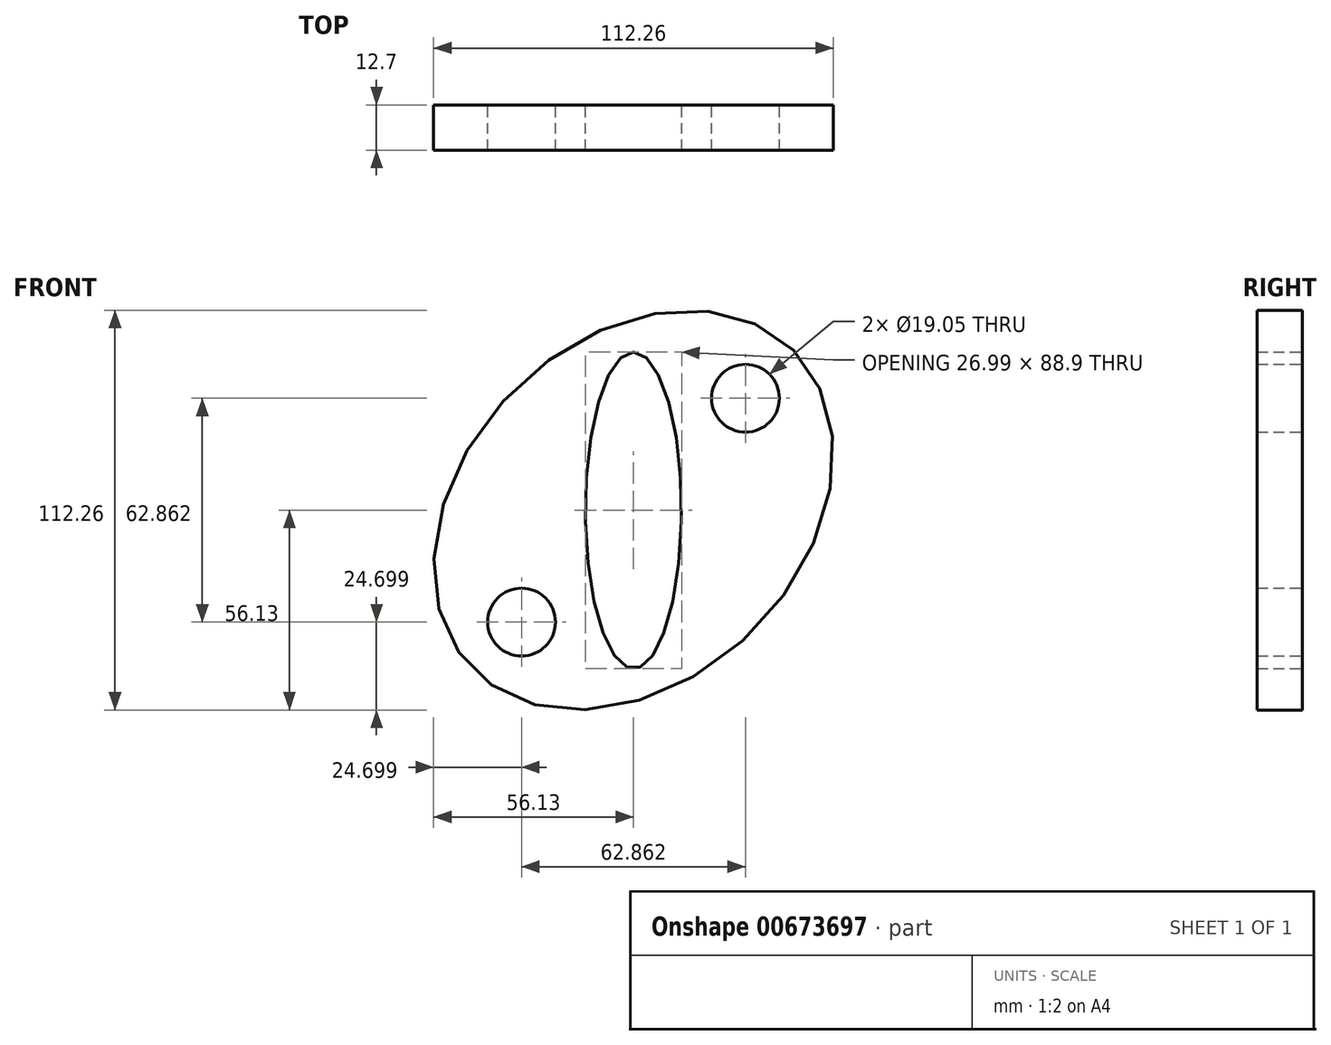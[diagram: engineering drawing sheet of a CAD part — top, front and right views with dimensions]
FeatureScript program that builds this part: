
annotation { "Feature Type Name" : "Feature", "Feature Type Description" : "" }
export const myFeature = defineFeature(function(context is Context, id is Id, definition is map)
    precondition{}
    {
        {
            var Q0;
            Q0=qCreatedBy(makeId("Front.planeOp"),FACE);
            var sketch = newSketch(context, id + "F0", { "sketchPlane" : qUnion([Q0])});
            skEllipse(sketch, "E0", {"center": v(0, 0) * mm, "majorRadius": 44.45 * mm, "minorRadius": 13.5 * mm, "majorAxis": v(0, 1)});
            skLineSegment(sketch, "E1.bottom", {"start": v(6.35, 38.1) * mm, "end": v(-6.35, 38.1) * mm});
            skLineSegment(sketch, "E1.top", {"start": v(6.35, -38.1) * mm, "end": v(-6.35, -38.1) * mm});
            skLineSegment(sketch, "E1.left", {"start": v(6.35, 38.1) * mm, "end": v(6.35, -38.1) * mm});
            skLineSegment(sketch, "E1.right", {"start": v(-6.35, 38.1) * mm, "end": v(-6.35, -38.1) * mm});
            skEllipse(sketch, "E2", {"center": v(0, 0) * mm, "majorRadius": 63.5 * mm, "minorRadius": 47.63 * mm, "majorAxis": v(0.7, 0.7)});
            skCircle(sketch, "E3", {"center": v(-31.43, -31.43) * mm, "radius": 9.53 * mm});
            skCircle(sketch, "E4", {"center": v(31.43, 31.43) * mm, "radius": 9.53 * mm});
            skSolve(sketch);
        }
        {
            var Q0;
            Q0=makeQuery(id+"F0.imprint","IMPRINT",FACE,{"disambiguationData":[TD([[makeQuery(id+"F0.imprint","IMPRINT",EDGE,{"derivedFrom":sQuery(id+"F0.wireOp",EDGE,"E0")}),-1.0]])]});
            extrude(context, id + "F1", {"entities" : qUnion([Q0]), "depth" : 12.7 * mm, "offsetDistance" : 25.4 * mm});
        }
    });
